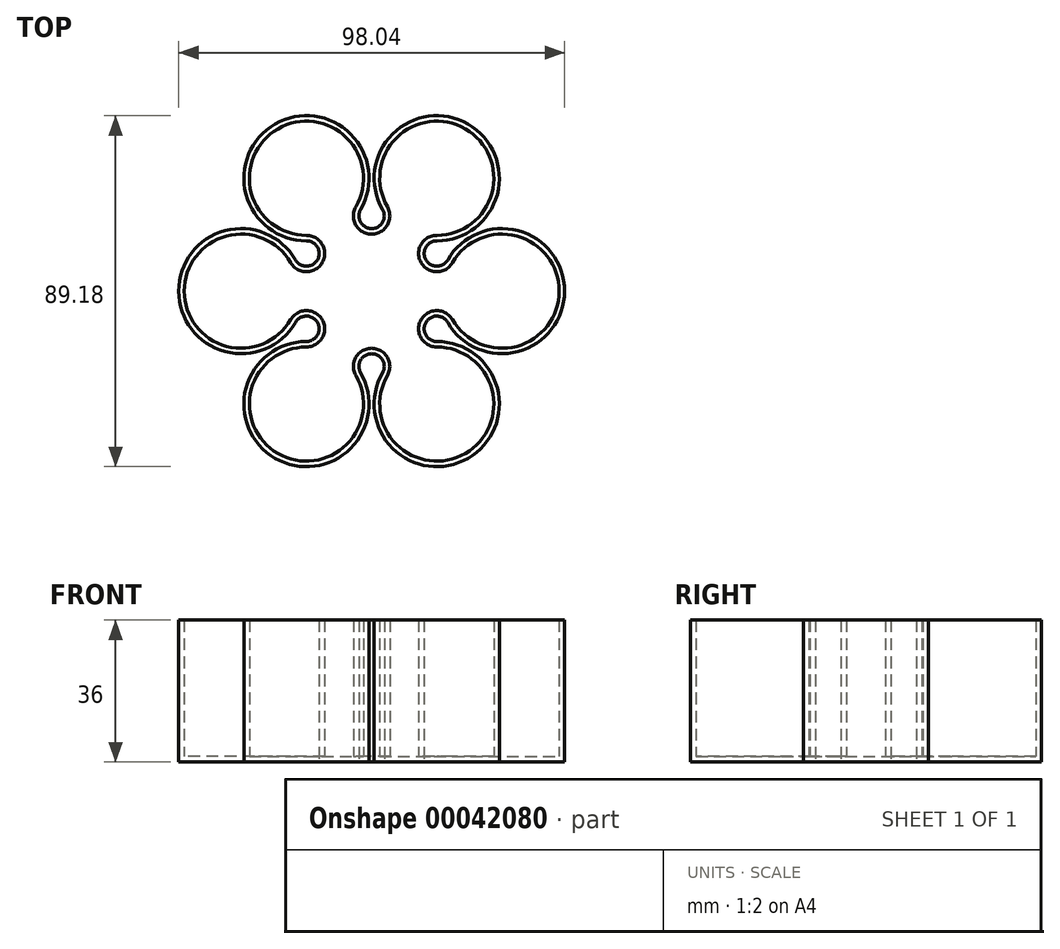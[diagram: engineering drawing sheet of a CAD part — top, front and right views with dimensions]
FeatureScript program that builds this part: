
annotation { "Feature Type Name" : "Feature", "Feature Type Description" : "" }
export const myFeature = defineFeature(function(context is Context, id is Id, definition is map)
    precondition{}
    {
        {
            var Q0;
            Q0=qCreatedBy(makeId("Top.planeOp"),FACE);
            var sketch = newSketch(context, id + "F0", { "sketchPlane" : qUnion([Q0])});
            skPoint(sketch, "E0.0.midPoint", {"position": v(17.67, 0) * mm});
            skLineSegment(sketch, "E1", {"start": v(0, 0) * mm, "end": v(-72.1, 0) * mm, "construction": true});
            skArc(sketch, "E2", {"start": v(-19.36, 7.95) * mm, "mid": v(-49.02, 0) * mm, "end": v(-19.36, -7.95) * mm});
            skArc(sketch, "E3.1.0", {"start": v(-16.56, -12.79) * mm, "mid": v(-24.51, -42.46) * mm, "end": v(-2.8, -20.74) * mm});
            skArc(sketch, "E3.2.0", {"start": v(2.8, -20.74) * mm, "mid": v(24.51, -42.46) * mm, "end": v(16.56, -12.79) * mm});
            skArc(sketch, "E3.3.0", {"start": v(19.36, -7.95) * mm, "mid": v(49.02, 0) * mm, "end": v(19.36, 7.95) * mm});
            skArc(sketch, "E3.4.0", {"start": v(16.56, 12.79) * mm, "mid": v(24.51, 42.46) * mm, "end": v(2.8, 20.74) * mm});
            skArc(sketch, "E3.5.0", {"start": v(-2.8, 20.74) * mm, "mid": v(-24.51, 42.46) * mm, "end": v(-16.56, 12.79) * mm});
            skPoint(sketch, "E3.center", {"position": v(0, 0) * mm});
            skLineSegment(sketch, "E4", {"start": v(0, 0) * mm, "end": v(-16.56, 28.69) * mm, "construction": true});
            skLineSegment(sketch, "E5", {"start": v(16.56, 28.69) * mm, "end": v(0, 0) * mm, "construction": true});
            skLineSegment(sketch, "E6", {"start": v(-16.56, 28.69) * mm, "end": v(16.56, 28.69) * mm, "construction": true});
            skLineSegment(sketch, "E7", {"start": v(16.56, 28.69) * mm, "end": v(-8.28, 14.34) * mm, "construction": true});
            skLineSegment(sketch, "E8", {"start": v(0, 0) * mm, "end": v(0, 28.69) * mm, "construction": true});
            skArc(sketch, "E9", {"start": v(-2.8, 20.74) * mm, "mid": v(0, 15.9) * mm, "end": v(2.8, 20.74) * mm});
            skArc(sketch, "E10.1.0", {"start": v(-19.36, 7.95) * mm, "mid": v(-13.77, 7.95) * mm, "end": v(-16.56, 12.79) * mm});
            skArc(sketch, "E10.2.0", {"start": v(-16.56, -12.79) * mm, "mid": v(-13.77, -7.95) * mm, "end": v(-19.36, -7.95) * mm});
            skArc(sketch, "E10.3.0", {"start": v(2.8, -20.74) * mm, "mid": v(0, -15.9) * mm, "end": v(-2.8, -20.74) * mm});
            skArc(sketch, "E10.4.0", {"start": v(19.36, -7.95) * mm, "mid": v(13.77, -7.95) * mm, "end": v(16.56, -12.79) * mm});
            skArc(sketch, "E10.5.0", {"start": v(16.56, 12.79) * mm, "mid": v(13.77, 7.95) * mm, "end": v(19.36, 7.95) * mm});
            skSolve(sketch);
        }
        {
            var Q0;
            Q0=makeQuery(id+"F0.imprint","IMPRINT",FACE,{"disambiguationData":[TD([[makeQuery(id+"F0.imprint","IMPRINT",EDGE,{"derivedFrom":sQuery(id+"F0.wireOp",EDGE,"E2")}),1.0]])]});
            extrude(context, id + "F1", {"entities" : qUnion([Q0]), "depth" : 36 * mm});
        }
        {
            var Q0;
            Q0=makeQuery(id+"F1.opExtrude","CAP_FACE",FACE,{"disambiguationData":[OSD([sQuery(id+"F0.wireOp",EDGE,"E2"),sQuery(id+"F0.wireOp",EDGE,"E3.1.0"),sQuery(id+"F0.wireOp",EDGE,"E3.2.0"),sQuery(id+"F0.wireOp",EDGE,"E3.3.0"),sQuery(id+"F0.wireOp",EDGE,"E3.4.0"),sQuery(id+"F0.wireOp",EDGE,"E3.5.0"),sQuery(id+"F0.wireOp",EDGE,"E9"),sQuery(id+"F0.wireOp",EDGE,"E10.1.0"),sQuery(id+"F0.wireOp",EDGE,"E10.2.0"),sQuery(id+"F0.wireOp",EDGE,"E10.3.0"),sQuery(id+"F0.wireOp",EDGE,"E10.4.0"),sQuery(id+"F0.wireOp",EDGE,"E10.5.0")])],"isStart":false});
            shell(context, id + "F2", {"entities" : qUnion([Q0]), "thickness" : 1.4 * mm});
        }
    });
